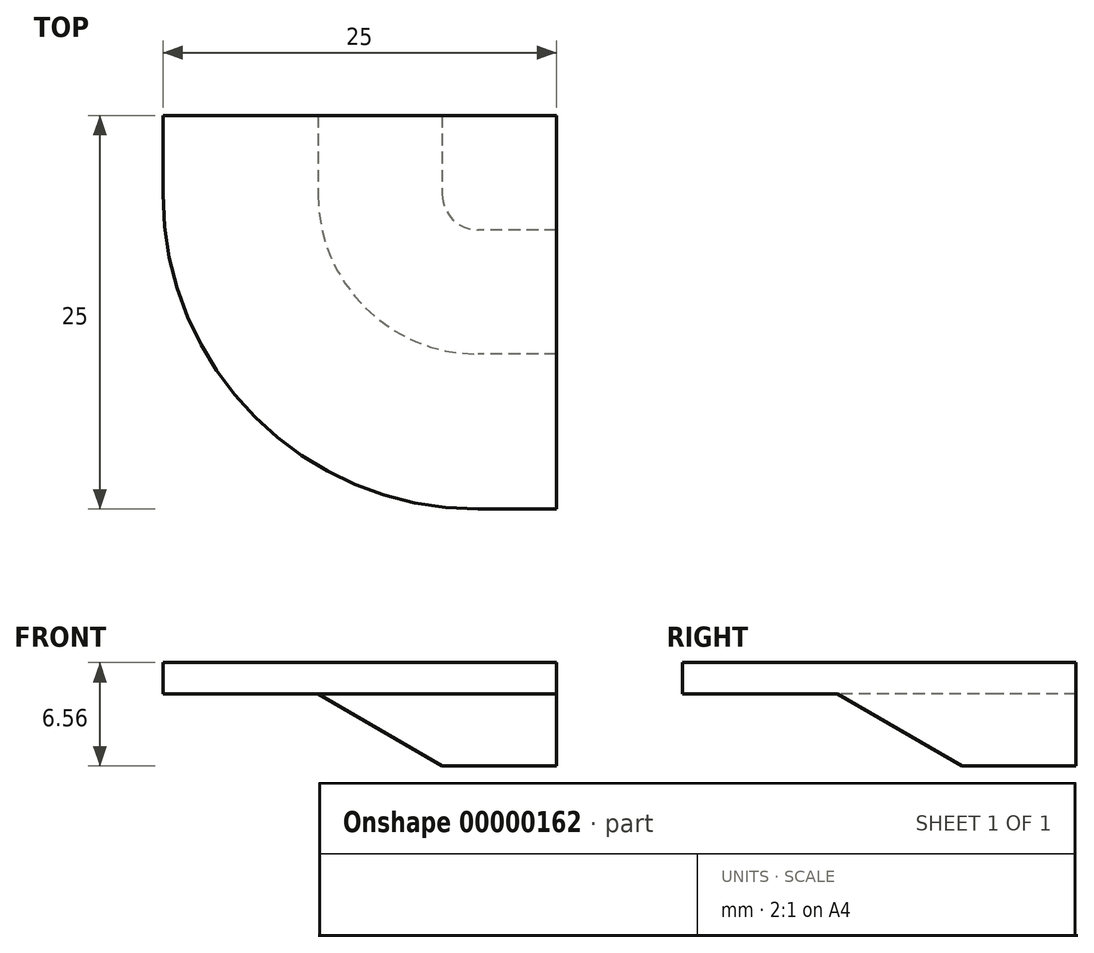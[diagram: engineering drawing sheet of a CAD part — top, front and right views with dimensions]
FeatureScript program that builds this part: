
annotation { "Feature Type Name" : "Feature", "Feature Type Description" : "" }
export const myFeature = defineFeature(function(context is Context, id is Id, definition is map)
    precondition{}
    {
        {
            var Q0;
            Q0  = qCreatedBy(makeId("Right.planeOp"), FACE);
            var sketch = newSketch(context, id + "F0", { "sketchPlane" : qUnion([Q0])});
            skLineSegment(sketch, "E0", {"start": v(0, 20) * mm, "end": v(-20, 20) * mm});
            skLineSegment(sketch, "E1", {"start": v(-20, 20) * mm, "end": v(-20, 18) * mm});
            skLineSegment(sketch, "E2", {"start": v(-20, 18) * mm, "end": v(-10.15, 18) * mm});
            skLineSegment(sketch, "E3", {"start": v(-10.15, 18) * mm, "end": v(-2.26, 13.44) * mm});
            skLineSegment(sketch, "E4", {"start": v(-2.26, 13.44) * mm, "end": v(0, 13.44) * mm});
            skLineSegment(sketch, "E5.trimOffspring", {"start": v(0, 13.44) * mm, "end": v(0, 20) * mm});
            skSolve(sketch);
        }
        {
            var Q0;
            Q0=makeQuery(id+"F0.imprint","IMPRINT",FACE,{"disambiguationData":[TD([[makeQuery(id+"F0.imprint","IMPRINT",EDGE,{"derivedFrom":sQuery(id+"F0.wireOp",EDGE,"E0")}),1.0]])]});
            extrude(context, id + "F1", {"entities" : qUnion([Q0]), "depth" : 5 * mm});
        }
        {
            var Q0;
            Q0=makeQuery(id+"F0.imprint","IMPRINT",FACE,{"disambiguationData":[TD([[makeQuery(id+"F0.imprint","IMPRINT",EDGE,{"derivedFrom":sQuery(id+"F0.wireOp",EDGE,"E0")}),1.0]])]});
            var Q1;
            Q1=makeQuery(id+"F1.opExtrude","CAP_EDGE",EDGE,{"disambiguationData":[OSD([sQuery(id+"F0.wireOp",EDGE,"E5.trimOffspring")])],"isStart":true});
            revolve(context, id + "F2", {"operationType" : NewBodyOperationType.ADD, "entities" : qUnion([Q0]), "axis" : qUnion([Q1]), "revolveType" : RevolveType.ONE_DIRECTION, "oppositeDirection" : true, "angle" : 90 * degree});
        }
        {
            var Q0;
            {var subQ0=sQuery(id+"F0.wireOp",EDGE,"E5.trimOffspring");Q0=makeQuery(id+"F2.boolean.opBoolean","MERGE",FACE,{"derivedFrom":[makeQuery(id+"F1.opExtrude","SWEPT_FACE",FACE,{"disambiguationData":[OSD([subQ0])]}),makeQuery(id+"F2.opRevolve","CAP_FACE",FACE,{"disambiguationData":[OSD([sQuery(id+"F0.wireOp",EDGE,"E0"),sQuery(id+"F0.wireOp",EDGE,"E1"),sQuery(id+"F0.wireOp",EDGE,"E2"),sQuery(id+"F0.wireOp",EDGE,"E3"),sQuery(id+"F0.wireOp",EDGE,"E4"),subQ0])],"isStart":false})]});}
            extrude(context, id + "F3", {"entities" : qUnion([Q0]), "operationType" : NewBodyOperationType.ADD, "depth" : 5 * mm});
        }
    });
